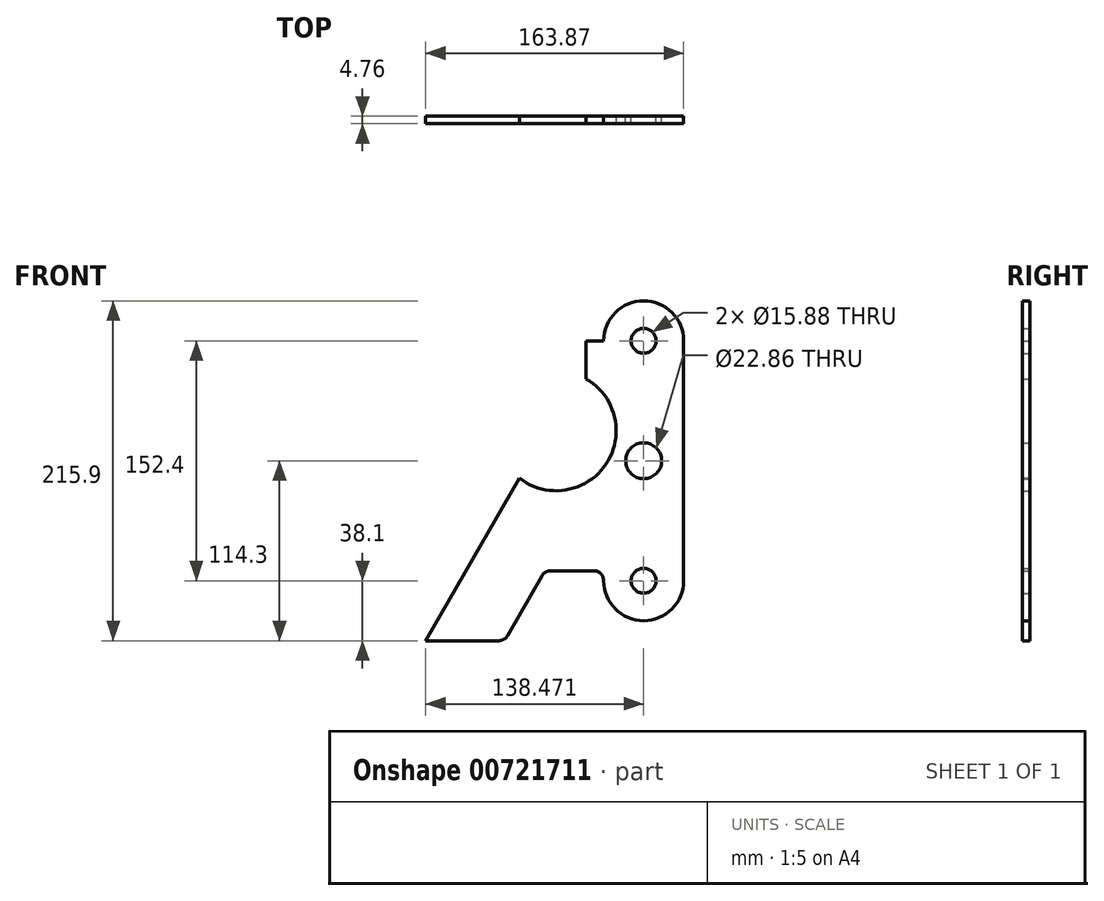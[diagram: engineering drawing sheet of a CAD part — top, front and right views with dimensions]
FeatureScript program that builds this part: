
annotation { "Feature Type Name" : "Feature", "Feature Type Description" : "" }
export const myFeature = defineFeature(function(context is Context, id is Id, definition is map)
    precondition{}
    {
        {
            var Q0;
            Q0=qCreatedBy(makeId("Front.planeOp"),FACE);
            var sketch = newSketch(context, id + "F0", { "sketchPlane" : qUnion([Q0])});
            skLineSegment(sketch, "E0", {"start": v(19, 57.15) * mm, "end": v(30.12, 57.15) * mm});
            skLineSegment(sketch, "E1", {"start": v(80.92, 57.15) * mm, "end": v(80.92, -95.25) * mm});
            skLineSegment(sketch, "E2", {"start": v(19, 57.15) * mm, "end": v(19, 33.02) * mm});
            skArc(sketch, "E3", {"start": v(19, 33.02) * mm, "mid": v(31.64, -21.22) * mm, "end": v(-23.34, -30.11) * mm});
            skArc(sketch, "E4", {"start": v(30.12, 57.15) * mm, "mid": v(55.52, 82.55) * mm, "end": v(80.92, 57.15) * mm});
            skCircle(sketch, "E5", {"center": v(55.52, 57.15) * mm, "radius": 7.94 * mm});
            skArc(sketch, "E6.MirrorCS", {"start": v(30.12, -95.25) * mm, "mid": v(55.52, -120.65) * mm, "end": v(80.92, -95.25) * mm});
            skCircle(sketch, "E7.MirrorC", {"center": v(55.52, -95.25) * mm, "radius": 7.94 * mm});
            skLineSegment(sketch, "E8", {"start": v(23.77, -88.9) * mm, "end": v(-3.5, -88.9) * mm});
            skLineSegment(sketch, "E9", {"start": v(-9, -92.07) * mm, "end": v(-31, -130.18) * mm});
            skPoint(sketch, "E10.visualSharp", {"position": v(30.93, -88.9) * mm});
            skArc(sketch, "E10.filletArc", {"start": v(30.12, -95.25) * mm, "mid": v(28.26, -90.76) * mm, "end": v(23.77, -88.9) * mm});
            skPoint(sketch, "E11.visualSharp", {"position": v(-7.17, -88.9) * mm});
            skArc(sketch, "E11.filletArc", {"start": v(-3.5, -88.9) * mm, "mid": v(-6.68, -89.75) * mm, "end": v(-9, -92.07) * mm});
            skLineSegment(sketch, "E12", {"start": v(-23.34, -30.11) * mm, "end": v(-82.95, -133.35) * mm});
            skLineSegment(sketch, "E13", {"start": v(-82.95, -133.35) * mm, "end": v(-36.5, -133.35) * mm});
            skLineSegment(sketch, "E14", {"start": v(55.52, 82.55) * mm, "end": v(55.52, -120.65) * mm, "construction": true});
            skPoint(sketch, "E14.startSnap0", {"position": v(55.52, 82.55) * mm});
            skLineSegment(sketch, "E15", {"start": v(-23.34, -30.11) * mm, "end": v(19, 33.02) * mm, "construction": true});
            skLineSegment(sketch, "E16", {"start": v(-111.48, -49.16) * mm, "end": v(99.09, -49.16) * mm, "construction": true});
            skPoint(sketch, "E17.visualSharp", {"position": v(-32.84, -133.35) * mm});
            skArc(sketch, "E17.filletArc", {"start": v(-36.5, -133.35) * mm, "mid": v(-33.33, -132.5) * mm, "end": v(-31, -130.18) * mm});
            skCircle(sketch, "E18", {"center": v(55.52, -19.05) * mm, "radius": 11.43 * mm});
            skLineSegment(sketch, "E19", {"start": v(4.66, 57.15) * mm, "end": v(90.42, 57.15) * mm, "construction": true});
            skLineSegment(sketch, "E20", {"start": v(80.92, -95.25) * mm, "end": v(14.37, -95.25) * mm, "construction": true});
            skSolve(sketch);
        }
        {
            var Q0;
            Q0=qSketchRegion(id+"F0",true);
            extrude(context, id + "F1", {"entities" : qUnion([Q0]), "depth" : 4.76 * mm, "offsetDistance" : 25.4 * mm});
        }
    });
